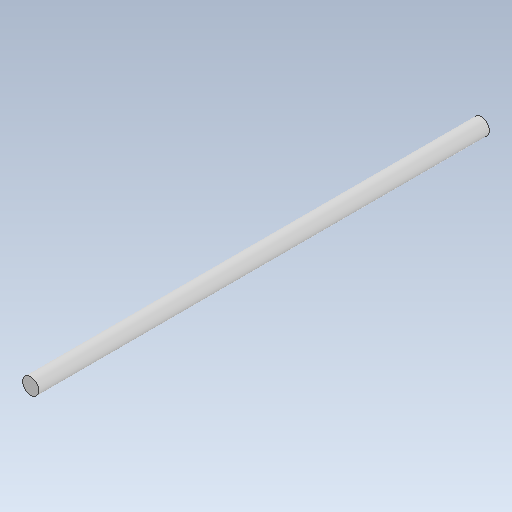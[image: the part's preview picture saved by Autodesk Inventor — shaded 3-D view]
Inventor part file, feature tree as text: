
AUTODESK INVENTOR PART (.ipt)
format: ipt  version: 2020 (Build 240168000, 168)  size: 83,968 bytes
history: native  units: mm
features: extrude x1, sketch x1
ambient origin geometry x8: Origin, YZ Plane, XZ Plane, XY Plane, X Axis, Y Axis, Z Axis, Center Point
bodies: Solid1 (feature_tree)
feature tree (2):
  extrude  "Extrusion1"  Depth=222.5mm TaperAngle=0.0deg
  sketch  "Sketch1"  dims[d0=8.0mm d1=222.5mm d2=0.0mm]
